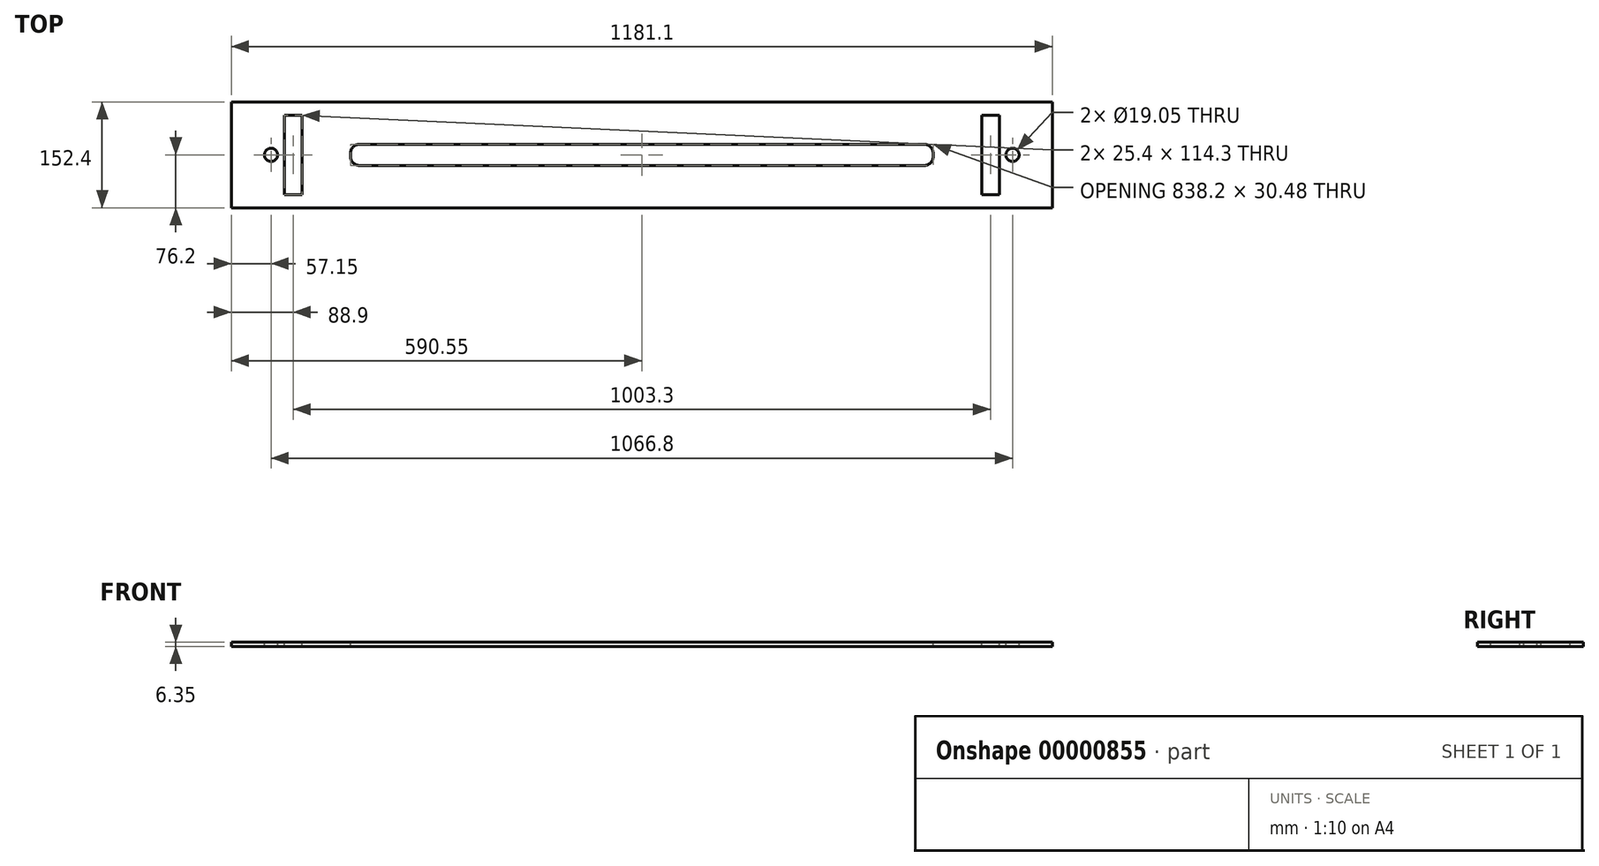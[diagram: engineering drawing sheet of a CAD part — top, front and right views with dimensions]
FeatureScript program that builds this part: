
annotation { "Feature Type Name" : "Feature", "Feature Type Description" : "" }
export const myFeature = defineFeature(function(context is Context, id is Id, definition is map)
    precondition{}
    {
        {
            var Q0;
            Q0=qCreatedBy(makeId("Top.planeOp"),FACE);
            var sketch = newSketch(context, id + "F0", { "sketchPlane" : qUnion([Q0])});
            skLineSegment(sketch, "E0.bottom", {"start": v(-590.55, 76.2) * mm, "end": v(0, 76.2) * mm});
            skLineSegment(sketch, "E0.top", {"start": v(-590.55, -76.2) * mm, "end": v(0, -76.2) * mm});
            skLineSegment(sketch, "E0.left", {"start": v(-590.55, 76.2) * mm, "end": v(-590.55, -76.2) * mm});
            skLineSegment(sketch, "E0.right", {"start": v(0, 76.2) * mm, "end": v(0, 15.24) * mm});
            skLineSegment(sketch, "E1", {"start": v(0, 124.51) * mm, "end": v(0, -154.97) * mm, "construction": true});
            skLineSegment(sketch, "E2", {"start": v(-505.67, 0) * mm, "end": v(510.2, 0) * mm, "construction": true});
            skLineSegment(sketch, "E3.bottom", {"start": v(-514.35, 57.15) * mm, "end": v(-488.95, 57.15) * mm});
            skLineSegment(sketch, "E3.top", {"start": v(-514.35, -57.15) * mm, "end": v(-488.95, -57.15) * mm});
            skLineSegment(sketch, "E3.left", {"start": v(-514.35, 57.15) * mm, "end": v(-514.35, -57.15) * mm});
            skLineSegment(sketch, "E3.right", {"start": v(-488.95, 57.15) * mm, "end": v(-488.95, -57.15) * mm});
            skCircle(sketch, "E4", {"center": v(-533.4, 0) * mm, "radius": 9.53 * mm});
            skLineSegment(sketch, "E5.bottom", {"start": v(-406.4, 15.24) * mm, "end": v(0, 15.24) * mm});
            skLineSegment(sketch, "E5.top", {"start": v(-406.4, -15.24) * mm, "end": v(0, -15.24) * mm});
            skLineSegment(sketch, "E5.left", {"start": v(-419.1, 2.54) * mm, "end": v(-419.1, -2.54) * mm});
            skLineSegment(sketch, "E6.trimOffspring", {"start": v(0, -15.24) * mm, "end": v(0, -76.2) * mm});
            skPoint(sketch, "E7.visualSharp", {"position": v(-419.1, 15.24) * mm});
            skArc(sketch, "E7.filletArc", {"start": v(-406.4, 15.24) * mm, "mid": v(-415.38, 11.52) * mm, "end": v(-419.1, 2.54) * mm});
            skPoint(sketch, "E8.visualSharp", {"position": v(-419.1, -15.24) * mm});
            skArc(sketch, "E8.filletArc", {"start": v(-419.1, -2.54) * mm, "mid": v(-415.38, -11.52) * mm, "end": v(-406.4, -15.24) * mm});
            skSolve(sketch);
        }
        {
            var Q0;
            Q0=makeQuery(id+"F0.imprint","IMPRINT",FACE,{"disambiguationData":[TD([[makeQuery(id+"F0.imprint","IMPRINT",EDGE,{"derivedFrom":sQuery(id+"F0.wireOp",EDGE,"E0.bottom")}),-1.0]])]});
            extrude(context, id + "F1", {"entities" : qUnion([Q0]), "oppositeDirection" : true, "depth" : 6.35 * mm});
        }
        {
            var Q0;
            Q0=makeQuery(id+"F1.opExtrude","SWEPT_BODY",BODY,{"disambiguationData":[OSD([sQuery(id+"F0.wireOp",EDGE,"E0.bottom"),sQuery(id+"F0.wireOp",EDGE,"E0.top"),sQuery(id+"F0.wireOp",EDGE,"E0.left"),sQuery(id+"F0.wireOp",EDGE,"E0.right"),sQuery(id+"F0.wireOp",EDGE,"E3.bottom"),sQuery(id+"F0.wireOp",EDGE,"E3.top"),sQuery(id+"F0.wireOp",EDGE,"E3.left"),sQuery(id+"F0.wireOp",EDGE,"E3.right"),sQuery(id+"F0.wireOp",EDGE,"E4")])]});
            var Q1;
            Q1=makeQuery(id+"F1.opExtrude","SWEPT_FACE",FACE,{"disambiguationData":[OSD([sQuery(id+"F0.wireOp",EDGE,"E0.right")])]});
            mirror(context, id + "F2", {"operationType" : NewBodyOperationType.ADD, "entities" : qUnion([Q0]), "mirrorPlane" : qUnion([Q1])});
        }
    });
